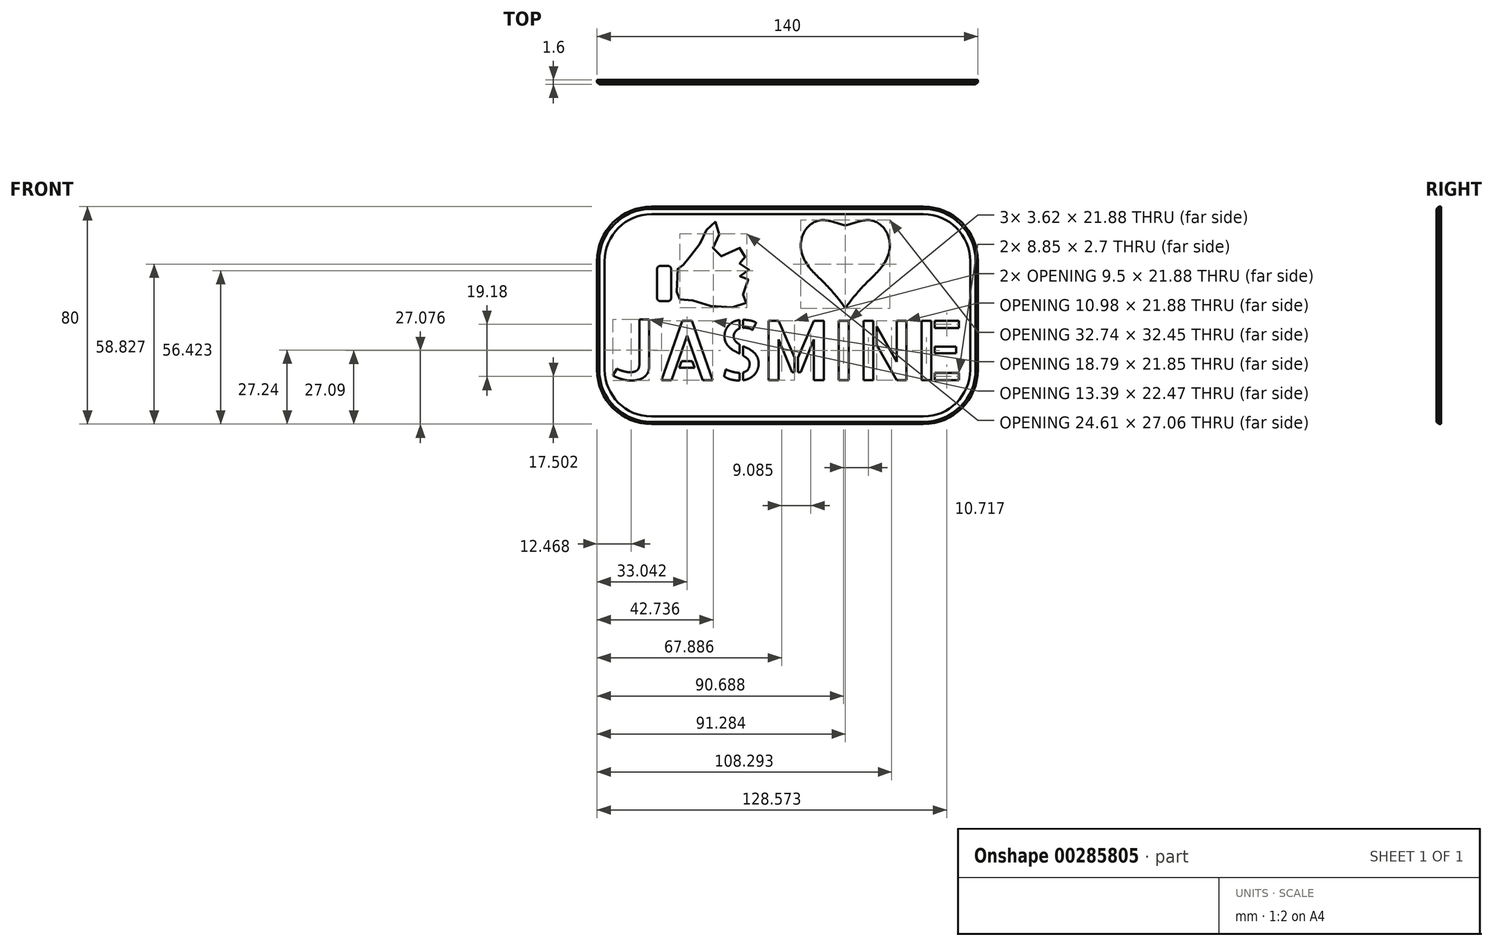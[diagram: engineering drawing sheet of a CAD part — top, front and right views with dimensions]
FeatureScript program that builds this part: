
annotation { "Feature Type Name" : "Feature", "Feature Type Description" : "" }
export const myFeature = defineFeature(function(context is Context, id is Id, definition is map)
    precondition{}
    {
        {
            var Q0;
            Q0=qCreatedBy(makeId("Front.planeOp"),FACE);
            var sketch = newSketch(context, id + "F0", { "sketchPlane" : qUnion([Q0])});
            skLineSegment(sketch, "E0.bottom", {"start": v(-70, 60) * mm, "end": v(70, 60) * mm});
            skLineSegment(sketch, "E0.top", {"start": v(-70, -20) * mm, "end": v(70, -20) * mm});
            skLineSegment(sketch, "E0.left", {"start": v(-70, 60) * mm, "end": v(-70, -20) * mm});
            skLineSegment(sketch, "E0.right", {"start": v(70, 60) * mm, "end": v(70, -20) * mm});
            skSolve(sketch);
        }
        {
            var Q0;
            Q0=qSketchRegion(id+"F0",true);
            extrude(context, id + "F1", {"entities" : qUnion([Q0]), "depth" : 1.6 * mm});
        }
        {
            var Q0;
            Q0=makeQuery(id+"F1.opExtrude","CAP_FACE",FACE,{"disambiguationData":[OSD([sQuery(id+"F0.wireOp",EDGE,"E0.bottom"),sQuery(id+"F0.wireOp",EDGE,"E0.top"),sQuery(id+"F0.wireOp",EDGE,"E0.left"),sQuery(id+"F0.wireOp",EDGE,"E0.right")])],"isStart":false});
            var sketch = newSketch(context, id + "F2", { "sketchPlane" : qUnion([Q0])});
            skText(sketch, "E1", { "text": "JASMINE", "fontName": "AllertaStencil-Regular.ttf"});
            skText(sketch, "E2", { "text": "♥", "fontName": "NotoSansCJKjp-Regular.otf"});
            const initialGuessF2  = {"E1": [-0.065, -0.00385, 1, 0, 0.02189], "E2": [0.00184, 0.0241, 1, 0, 0.028]};
            skSetInitialGuess(sketch, initialGuessF2);
            skSolve(sketch);
        }
        {
            var Q0;
            Q0=qSketchRegion(id+"F2",true);
            extrude(context, id + "F3", {"entities" : qUnion([Q0]), "operationType" : NewBodyOperationType.REMOVE, "endBound" : BoundingType.THROUGH_ALL, "oppositeDirection" : true, "depth" : 25 * mm});
        }
        {
            var Q0;
            Q0=makeQuery(id+"F1.opExtrude","SWEPT_EDGE",EDGE,{"disambiguationData":[OSD([sQuery(id+"F0.wireOp",EDGE,"E0.top"),sQuery(id+"F0.wireOp",EDGE,"E0.right")])]});
            var Q1;
            Q1=makeQuery(id+"F1.opExtrude","SWEPT_EDGE",EDGE,{"disambiguationData":[OSD([sQuery(id+"F0.wireOp",EDGE,"E0.bottom"),sQuery(id+"F0.wireOp",EDGE,"E0.right")])]});
            var Q2;
            Q2=makeQuery(id+"F1.opExtrude","SWEPT_EDGE",EDGE,{"disambiguationData":[OSD([sQuery(id+"F0.wireOp",EDGE,"E0.top"),sQuery(id+"F0.wireOp",EDGE,"E0.left")])]});
            var Q3;
            Q3=makeQuery(id+"F1.opExtrude","SWEPT_EDGE",EDGE,{"disambiguationData":[OSD([sQuery(id+"F0.wireOp",EDGE,"E0.bottom"),sQuery(id+"F0.wireOp",EDGE,"E0.left")])]});
            fillet(context, id + "F4", {"entities" : qUnion([Q0, Q1, Q2, Q3]), "radius" : 20 * mm, "tangentPropagation" : true, "allowEdgeOverflow" : false});
        }
        {
            var Q0;
            Q0=makeQuery(id+"F1.opExtrude","CAP_EDGE",EDGE,{"disambiguationData":[OSD([sQuery(id+"F0.wireOp",EDGE,"E0.top")])],"isStart":false});
            chamfer(context, id + "F5", {"entities" : qUnion([Q0]), "width" : 0.8 * mm, "tangentPropagation" : true});
        }
        {
            var Q0;
            Q0=makeQuery(id+"F1.opExtrude","CAP_FACE",FACE,{"disambiguationData":[OSD([sQuery(id+"F0.wireOp",EDGE,"E0.bottom"),sQuery(id+"F0.wireOp",EDGE,"E0.top"),sQuery(id+"F0.wireOp",EDGE,"E0.left"),sQuery(id+"F0.wireOp",EDGE,"E0.right")])],"isStart":false});
            var sketch = newSketch(context, id + "F6", { "sketchPlane" : qUnion([Q0])});
            skLineSegment(sketch, "E3.0", {"start": v(-50, -17.2) * mm, "end": v(50, -17.2) * mm});
            skArc(sketch, "E3.1", {"start": v(-67.2, 0) * mm, "mid": v(-62.16, -12.16) * mm, "end": v(-50, -17.2) * mm});
            skArc(sketch, "E3.2", {"start": v(50, -17.2) * mm, "mid": v(62.16, -12.16) * mm, "end": v(67.2, 0) * mm});
            skLineSegment(sketch, "E3.3", {"start": v(-67.2, 40) * mm, "end": v(-67.2, 0) * mm});
            skLineSegment(sketch, "E3.4", {"start": v(67.2, 0) * mm, "end": v(67.2, 40) * mm});
            skArc(sketch, "E3.5", {"start": v(67.2, 40) * mm, "mid": v(62.16, 52.16) * mm, "end": v(50, 57.2) * mm});
            skLineSegment(sketch, "E3.6", {"start": v(50, 57.2) * mm, "end": v(-50, 57.2) * mm});
            skArc(sketch, "E3.7", {"start": v(-50, 57.2) * mm, "mid": v(-62.16, 52.16) * mm, "end": v(-67.2, 40) * mm});
            skSolve(sketch);
        }
        {
            var Q0;
            Q0=qSketchRegion(id+"F6",true);
            extrude(context, id + "F7", {"entities" : qUnion([Q0]), "operationType" : NewBodyOperationType.REMOVE, "oppositeDirection" : true, "depth" : 0.4 * mm});
        }
        {
            var Q0;
            Q0=makeQuery(id+"F7.boolean.opBoolean","COPY",FACE,{"derivedFrom":makeQuery(id+"F7.opExtrude","CAP_FACE",FACE,{"disambiguationData":[OSD([sQuery(id+"F6.wireOp",EDGE,"E3.0"),sQuery(id+"F6.wireOp",EDGE,"E3.1"),sQuery(id+"F6.wireOp",EDGE,"E3.2"),sQuery(id+"F6.wireOp",EDGE,"E3.3"),sQuery(id+"F6.wireOp",EDGE,"E3.4"),sQuery(id+"F6.wireOp",EDGE,"E3.5"),sQuery(id+"F6.wireOp",EDGE,"E3.6"),sQuery(id+"F6.wireOp",EDGE,"E3.7")])],"isStart":false})});
            var sketch = newSketch(context, id + "F8", { "sketchPlane" : qUnion([Q0])});
            skLineSegment(sketch, "E4", {"start": v(26.91, 54.7) * mm, "end": v(21.28, 53.06) * mm});
            skLineSegment(sketch, "E5", {"start": v(21.28, 53.06) * mm, "end": v(15.64, 54.7) * mm});
            skLineSegment(sketch, "E6", {"start": v(15.64, 54.7) * mm, "end": v(15.22, 47.04) * mm});
            skLineSegment(sketch, "E7", {"start": v(15.22, 47.04) * mm, "end": v(26.88, 46.4) * mm});
            skLineSegment(sketch, "E8", {"start": v(26.88, 46.4) * mm, "end": v(26.91, 54.7) * mm});
            skSolve(sketch);
        }
        {
            var Q0;
            Q0 = qSketchRegion(id + "F8", true);
            extrude(context, id + "F9", {"entities" : qUnion([Q0]), "operationType" : NewBodyOperationType.REMOVE, "oppositeDirection" : true, "depth" : 25 * mm});
        }
        {
            var Q0;
            Q0=makeQuery(id+"F7.boolean.opBoolean","COPY",FACE,{"derivedFrom":makeQuery(id+"F7.opExtrude","CAP_FACE",FACE,{"disambiguationData":[OSD([sQuery(id+"F6.wireOp",EDGE,"E3.0"),sQuery(id+"F6.wireOp",EDGE,"E3.1"),sQuery(id+"F6.wireOp",EDGE,"E3.2"),sQuery(id+"F6.wireOp",EDGE,"E3.3"),sQuery(id+"F6.wireOp",EDGE,"E3.4"),sQuery(id+"F6.wireOp",EDGE,"E3.5"),sQuery(id+"F6.wireOp",EDGE,"E3.6"),sQuery(id+"F6.wireOp",EDGE,"E3.7")])],"isStart":false})});
            var sketch = newSketch(context, id + "F10", { "sketchPlane" : qUnion([Q0])});
            skFitSpline(sketch, "E9", {"points": [v(-39.57, 25.93) * mm, v(-40.32, 26.28) * mm, v(-40.6, 27.2) * mm, v(-40.34, 37.25) * mm, v(-40.19, 37.43) * mm, v(-39.33, 37.55) * mm, v(-37.33, 39.73) * mm, v(-35.58, 41.85) * mm, v(-32.38, 46.04) * mm, v(-30.1, 50.4) * mm, v(-27.74, 54.55) * mm, v(-24.91, 52.7) * mm, v(-26.13, 47.63) * mm, v(-27.4, 44) * mm, v(-24.51, 41.68) * mm, v(-16.78, 44.91) * mm, v(-15.22, 42.03) * mm, v(-17.82, 39.5) * mm, v(-17.82, 39.12) * mm, v(-14.65, 38.45) * mm, v(-14.82, 35.4) * mm, v(-17.49, 34.42) * mm, v(-17.49, 34.07) * mm, v(-14.53, 33.32) * mm, v(-14.59, 29.91) * mm, v(-17.58, 28.6) * mm, v(-17.53, 28.24) * mm, v(-14.53, 26.51) * mm, v(-15.34, 24.5) * mm, v(-19.6, 23) * mm, v(-30, 23.86) * mm, v(-36.28, 25.88) * mm, v(-39.57, 25.93) * mm]});
            skLineSegment(sketch, "E10.bottom", {"start": v(-43.8, 38.15) * mm, "end": v(-46.9, 38.15) * mm});
            skLineSegment(sketch, "E10.top", {"start": v(-43.8, 25.28) * mm, "end": v(-46.9, 25.28) * mm});
            skLineSegment(sketch, "E10.left", {"start": v(-42.8, 37.15) * mm, "end": v(-42.8, 26.28) * mm});
            skLineSegment(sketch, "E10.right", {"start": v(-47.9, 37.15) * mm, "end": v(-47.9, 26.28) * mm});
            skPoint(sketch, "E11.visualSharp", {"position": v(-42.8, 38.15) * mm});
            skArc(sketch, "E11.filletArc", {"start": v(-42.8, 37.15) * mm, "mid": v(-43.1, 37.86) * mm, "end": v(-43.8, 38.15) * mm});
            skPoint(sketch, "E12.visualSharp", {"position": v(-47.9, 38.15) * mm});
            skArc(sketch, "E12.filletArc", {"start": v(-46.9, 38.15) * mm, "mid": v(-47.6, 37.86) * mm, "end": v(-47.9, 37.15) * mm});
            skPoint(sketch, "E13.visualSharp", {"position": v(-47.9, 25.28) * mm});
            skArc(sketch, "E13.filletArc", {"start": v(-47.9, 26.28) * mm, "mid": v(-47.6, 25.57) * mm, "end": v(-46.9, 25.28) * mm});
            skPoint(sketch, "E14.visualSharp", {"position": v(-42.8, 25.28) * mm});
            skArc(sketch, "E14.filletArc", {"start": v(-43.8, 25.28) * mm, "mid": v(-43.1, 25.57) * mm, "end": v(-42.8, 26.28) * mm});
            skSolve(sketch);
        }
        {
            var Q0;
            Q0 = qSketchRegion(id + "F10", true);
            extrude(context, id + "F11", {"entities" : qUnion([Q0]), "operationType" : NewBodyOperationType.REMOVE, "endBound" : BoundingType.THROUGH_ALL, "oppositeDirection" : true, "depth" : 25 * mm});
        }
    });
